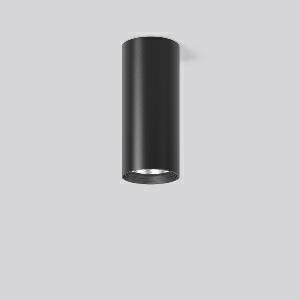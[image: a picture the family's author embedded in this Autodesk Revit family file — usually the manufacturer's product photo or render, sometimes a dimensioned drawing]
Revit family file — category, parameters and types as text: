
# Revit family: heledon_mini_a_931210_003_1_29a2
name_source: partatom
category: Lighting Fixtures
units: mm (PartAtom-declared; Revit-internal decimal feet)

## family parameters
Cut with Voids When Loaded = No
Host = Face
Light Source = No
Part Type = Normal
Room Calculation Point = No
Round Connector Dimension = Use Diameter
Shared = No

## types (1)
- HELEDON mini A (1 x LED Modul 940, 3900 lm, 4000)
    Apparent Load = 29 VA
    Approval mark = CE
    CIE Flux Codes = 95 99 100 100 100
    Color Rendering = 92
    Color Temperature = 4000
    Default Elevation = 1800 mm
    Description = Series: HELEDON mini
Cylindrical surface-mounted downlight. Housing: die-cast aluminium, powder-coated. Internal ceiling frame polycarbonate with bayonet mounting. Black plastic ring and recessed LED to prevent glare from the side. Optical assembly with reflector made of MIRO-Silver with 98% total light reflection for outstanding efficiency - can be changed without tools. Best colour rendering index Ra>90. Suitable for Ceiling mounting. Easy installation with a separate ceiling frame with bayonet mounting and plug connection. Driver integrated. Connected via plug-in connector. High quality converter without flickering and stroboscopic effect. The following accessories can be mounted without use of tools: interchangeable lenses, decorative glasses, honeycomb louvre, clear and frosted diffusers, white interchangeable plastic ring. 
Colour: deep black, matt (RAL 9005)
Diameter: 87 mm
Height: 197 mm
Lamp: LED
Socket: without socket
Colour temperature: 4000K
Colour rendering index (CRI): 92
System power: 29 W
Rated luminous flux: 3900 lm
Luminous efficiency: 134 lm/W
Control gear: Regulated power supply
Protection class: I
Type of protection: IP 20
    Height = 197 mm
    Lamp = 1 x LED Modul 940
    Lamp Light Flux = 3900 lm
    Lamp count = 1
    Length = 87 mm
    Lifetime = 50000 h
    Luminous efficacy = 134 lm/W
    Manufacturer = RZB
    ModVariant = No
    Model = 931210.003.1
    Mounting Place = Ceiling
    Mounting Type = Surface mounted
    Number of Poles = 1
    OnlyDefault = Yes
    Power Factor = 1
    Product Name = HELEDON mini A
    Product group = Surface mounted downlights
    ProductGroupID = 302
    Protection Class = Protection class I
    Protection Degree = IP 20
    RLX_Detail_Level = 1
    RLX_Emergency_Light_Flux = 0 lm
    RLX_Emergency_Type = 0
    RLX_Emergency_Type_DB = No
    RlxData = <blob elided: 108281 chars, md5=345c639f>
    Socket = socket
    Standby Power = 0 W
    System Light Flux = 3900 lm
    System Power = 29 W
    Type Comments = Product without accessories
    Type Image = 931188.003.jpg
    URL = http://relux.com
    VarID = ---
    Voltage = 230 V
    Voltage Range = 220-240 V
    Weight = 0.00 kg
    Width = 0 mm  [stored 0 ft]

note: [stored X ft] marks values corroborated as IEEE doubles in the binary element streams (Revit-internal decimal feet)

## geometry (parser evidence)
native form markers: Blend x4, Sweep x9
no freeform markers — native parametric forms only
